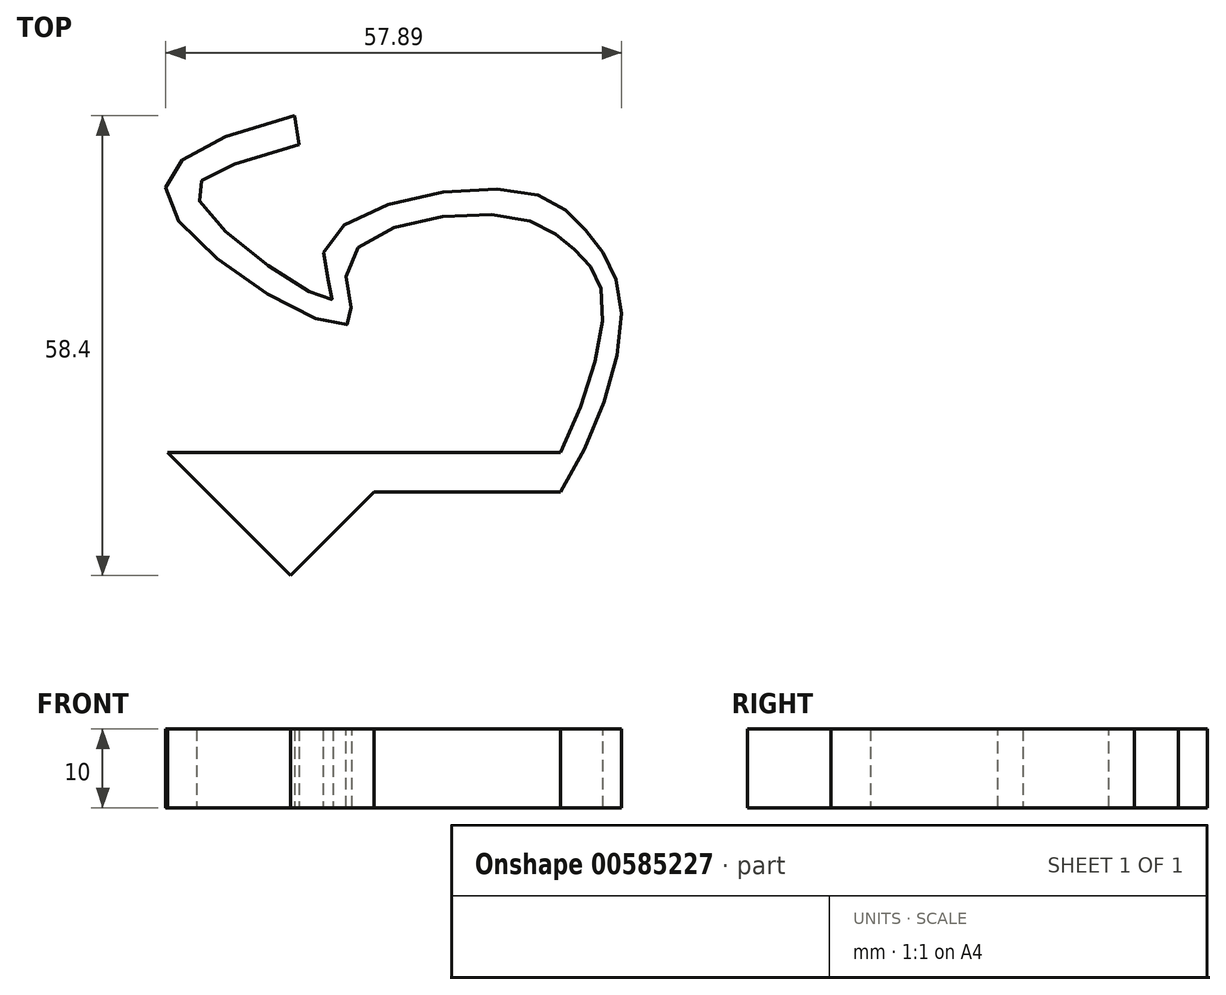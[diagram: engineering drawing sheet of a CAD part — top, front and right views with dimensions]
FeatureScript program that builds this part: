
annotation { "Feature Type Name" : "Feature", "Feature Type Description" : "" }
export const myFeature = defineFeature(function(context is Context, id is Id, definition is map)
    precondition{}
    {
        {
            var Q0;
            Q0=qCreatedBy(makeId("Top.planeOp"),FACE);
            var sketch = newSketch(context, id + "F0", { "sketchPlane" : qUnion([Q0])});
            skLineSegment(sketch, "E0.bottom", {"start": v(0, 0) * mm, "end": v(120, 0) * mm});
            skLineSegment(sketch, "E0.top", {"start": v(0, 80) * mm, "end": v(120, 80) * mm});
            skLineSegment(sketch, "E0.left", {"start": v(0, 0) * mm, "end": v(0, 80) * mm});
            skLineSegment(sketch, "E0.right", {"start": v(120, 0) * mm, "end": v(120, 80) * mm});
            skFitSpline(sketch, "E1", {"points": [v(65.6, 30.25) * mm, v(70.78, 50.69) * mm, v(67.3, 56.1) * mm, v(58.87, 60.3) * mm, v(38.66, 54.56) * mm, v(38.66, 46.62) * mm, v(16.34, 60.76) * mm, v(31.82, 73.05) * mm], "startDerivative": vector(65.51, 131.02) * mm, "endDerivative": vector(237.53, 59.1) * mm});
            skFitSpline(sketch, "E2", {"points": [v(65.6, 25.25) * mm, v(73.3, 48.75) * mm, v(69.04, 58.23) * mm, v(59.37, 63.65) * mm, v(35.6, 56.11) * mm, v(36.53, 49.72) * mm, v(20.14, 61.5) * mm, v(32.35, 69.4) * mm], "startDerivative": vector(74.44, 116.97) * mm, "endDerivative": vector(235.1, 67.91) * mm});
            skLineSegment(sketch, "E3", {"start": v(31.82, 73.05) * mm, "end": v(32.35, 69.4) * mm});
            skLineSegment(sketch, "E4", {"start": v(65.6, 25.25) * mm, "end": v(41.91, 25.25) * mm});
            skLineSegment(sketch, "E5", {"start": v(41.91, 25.25) * mm, "end": v(31.3, 14.65) * mm});
            skLineSegment(sketch, "E6", {"start": v(31.3, 14.65) * mm, "end": v(15.7, 30.25) * mm});
            skLineSegment(sketch, "E7", {"start": v(15.7, 30.25) * mm, "end": v(65.6, 30.25) * mm});
            skSolve(sketch);
        }
        {
            var Q0;
            Q0=makeQuery(id+"F0.imprint","IMPRINT",FACE,{"disambiguationData":[TD([[makeQuery(id+"F0.imprint","IMPRINT",EDGE,{"derivedFrom":sQuery(id+"F0.wireOp",EDGE,"E1")}),-1.0]])]});
            extrude(context, id + "F1", {"entities" : qUnion([Q0]), "depth" : 10 * mm, "offsetDistance" : 25 * mm});
        }
    });
